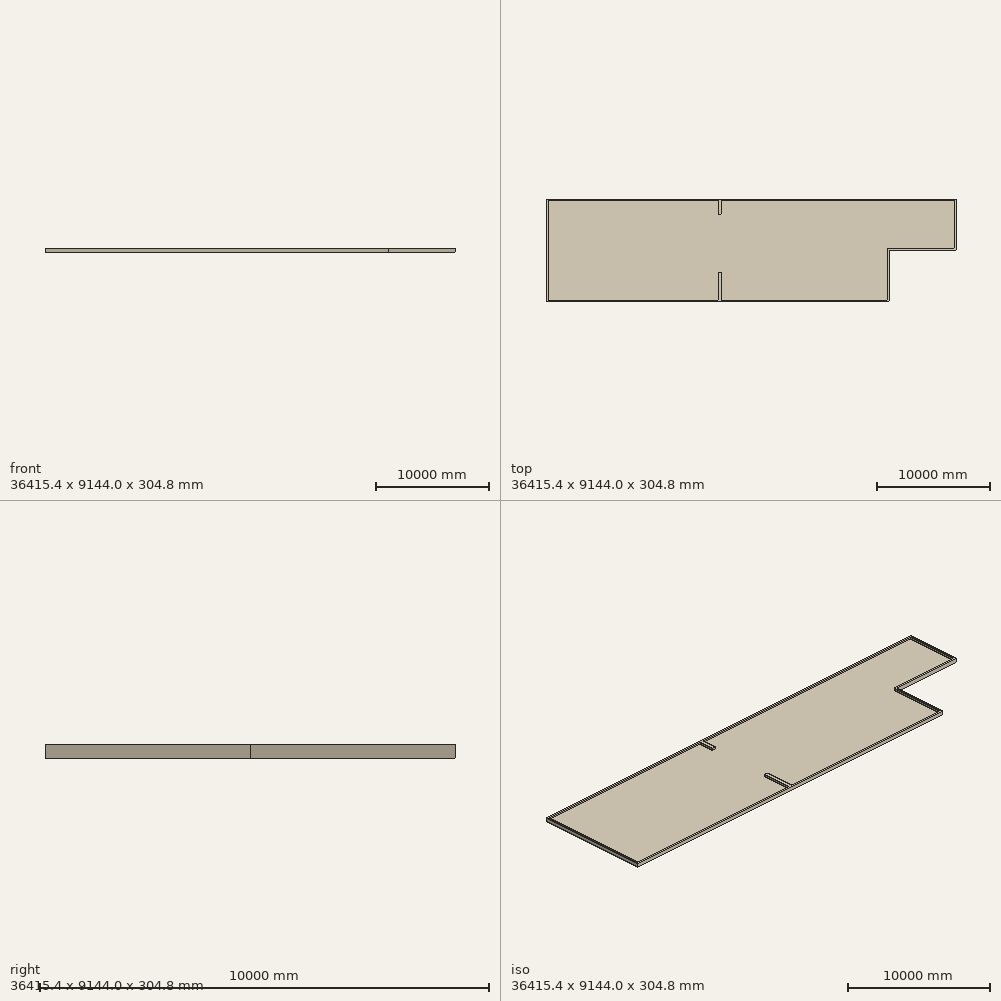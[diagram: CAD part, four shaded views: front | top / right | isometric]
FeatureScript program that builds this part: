
annotation { "Feature Type Name" : "Feature", "Feature Type Description" : "" }
export const myFeature = defineFeature(function(context is Context, id is Id, definition is map)
    precondition{}
    {
        {
            var Q0;
            Q0=qCreatedBy(makeId("Top.planeOp"),FACE);
            var sketch = newSketch(context, id + "F0", { "sketchPlane" : qUnion([Q0])});
            skLineSegment(sketch, "E0.bottom", {"start": v(0, 0) * mm, "end": v(30480, 0) * mm});
            skLineSegment(sketch, "E0.top", {"start": v(0, 9144) * mm, "end": v(30480, 9144) * mm});
            skLineSegment(sketch, "E0.left", {"start": v(0, 0) * mm, "end": v(0, 9144) * mm});
            skLineSegment(sketch, "E0.right", {"start": v(30480, 0) * mm, "end": v(30480, 4572) * mm});
            skLineSegment(sketch, "E1.bottom", {"start": v(30480, 9144) * mm, "end": v(36415.43, 9144) * mm});
            skLineSegment(sketch, "E1.top", {"start": v(30480, 4572) * mm, "end": v(36415.43, 4572) * mm});
            skLineSegment(sketch, "E1.right", {"start": v(36415.43, 9144) * mm, "end": v(36415.43, 4572) * mm});
            skSolve(sketch);
        }
        {
            var Q0;
            Q0 = qSketchRegion(id + "F0", true);
            extrude(context, id + "F1", {"entities" : qUnion([Q0]), "oppositeDirection" : true, "depth" : 304.8 * mm});
        }
        {
            var Q0;
            Q0=makeQuery(id+"F1.opExtrude","CAP_FACE",FACE,{"disambiguationData":[OSD([sQuery(id+"F0.wireOp",EDGE,"E0.bottom"),sQuery(id+"F0.wireOp",EDGE,"E0.top"),sQuery(id+"F0.wireOp",EDGE,"E0.left"),sQuery(id+"F0.wireOp",EDGE,"E0.right")])],"isStart":true});
            shell(context, id + "F2", {"entities" : qUnion([Q0]), "thickness" : 152.4 * mm});
        }
        {
            var Q0;
            Q0=makeQuery(id+"F2.opShell","OFFSET_FACE",FACE,{"disambiguationData":[OSD([sQuery(id+"F0.wireOp",EDGE,"E0.bottom"),sQuery(id+"F0.wireOp",EDGE,"E0.top"),sQuery(id+"F0.wireOp",EDGE,"E0.left"),sQuery(id+"F0.wireOp",EDGE,"E0.right")])]});
            var sketch = newSketch(context, id + "F3", { "sketchPlane" : qUnion([Q0])});
            skLineSegment(sketch, "E2", {"start": v(15240, 8991.6) * mm, "end": v(15240, 152.4) * mm});
            skLineSegment(sketch, "E3", {"start": v(15240, 8991.6) * mm, "end": v(15544.8, 8991.6) * mm});
            skLineSegment(sketch, "E4", {"start": v(15544.8, 8991.6) * mm, "end": v(15544.8, 152.4) * mm});
            skLineSegment(sketch, "E5", {"start": v(15544.8, 152.4) * mm, "end": v(15240, 152.4) * mm});
            skSolve(sketch);
        }
        {
            var Q0;
            Q0 = qSketchRegion(id + "F3", true);
            var Q1;
            Q1=makeQuery(id+"F1.opExtrude","CAP_FACE",FACE,{"disambiguationData":[OSD([sQuery(id+"F0.wireOp",EDGE,"E0.bottom"),sQuery(id+"F0.wireOp",EDGE,"E0.top"),sQuery(id+"F0.wireOp",EDGE,"E0.left"),sQuery(id+"F0.wireOp",EDGE,"E0.right")])],"isStart":true});
            extrude(context, id + "F4", {"entities" : qUnion([Q0]), "operationType" : NewBodyOperationType.ADD, "endBound" : BoundingType.UP_TO_SURFACE, "endBoundEntityFace" : qUnion([Q1]), "depth" : 25.4 * mm});
        }
        {
            var Q0;
            {var subQ0=sQuery(id+"F0.wireOp",EDGE,"E0.right");var subQ1=sQuery(id+"F0.wireOp",EDGE,"E0.left");var subQ2=sQuery(id+"F0.wireOp",EDGE,"E0.top");var subQ3=sQuery(id+"F0.wireOp",EDGE,"E0.bottom");Q0=makeQuery(id+"F4.boolean.opBoolean","MERGE",FACE,{"derivedFrom":[makeQuery(id+"F1.opExtrude","CAP_FACE",FACE,{"disambiguationData":[OSD([subQ3,subQ2,subQ1,subQ0])],"isStart":true}),makeQuery(id+"F4.opExtrude","CAP_FACE",FACE,{"disambiguationData":[OSD([subQ3,subQ2,subQ1,subQ0])],"isStart":false})]});}
            var sketch = newSketch(context, id + "F5", { "sketchPlane" : qUnion([Q0])});
            skLineSegment(sketch, "E6.bottom", {"start": v(15240, 7772.4) * mm, "end": v(15544.8, 7772.4) * mm});
            skLineSegment(sketch, "E6.top", {"start": v(15240, 2590.8) * mm, "end": v(15544.8, 2590.8) * mm});
            skLineSegment(sketch, "E6.left", {"start": v(15240, 7772.4) * mm, "end": v(15240, 2590.8) * mm});
            skLineSegment(sketch, "E6.right", {"start": v(15544.8, 7772.4) * mm, "end": v(15544.8, 2590.8) * mm});
            skSolve(sketch);
        }
        {
            var Q0;
            Q0 = qSketchRegion(id + "F5", true);
            var Q1;
            {var subQ0=sQuery(id+"F0.wireOp",EDGE,"E0.bottom");var subQ1=sQuery(id+"F0.wireOp",EDGE,"E0.top");var subQ2=sQuery(id+"F0.wireOp",EDGE,"E0.left");Q1=makeQuery(id+"F4.boolean.opBoolean","SPLIT",FACE,{"disambiguationData":[TD([makeQuery(id+"F2.opShell","OFFSET_FACE",FACE,{"disambiguationData":[OSD([subQ2])]})])],"derivedFrom":makeQuery(id+"F2.opShell","OFFSET_FACE",FACE,{"disambiguationData":[OSD([subQ0,subQ1,subQ2,sQuery(id+"F0.wireOp",EDGE,"E0.right")])]})});}
            extrude(context, id + "F6", {"entities" : qUnion([Q0]), "operationType" : NewBodyOperationType.REMOVE, "endBound" : BoundingType.UP_TO_SURFACE, "oppositeDirection" : true, "endBoundEntityFace" : qUnion([Q1]), "depth" : 25.4 * mm});
        }
    });
